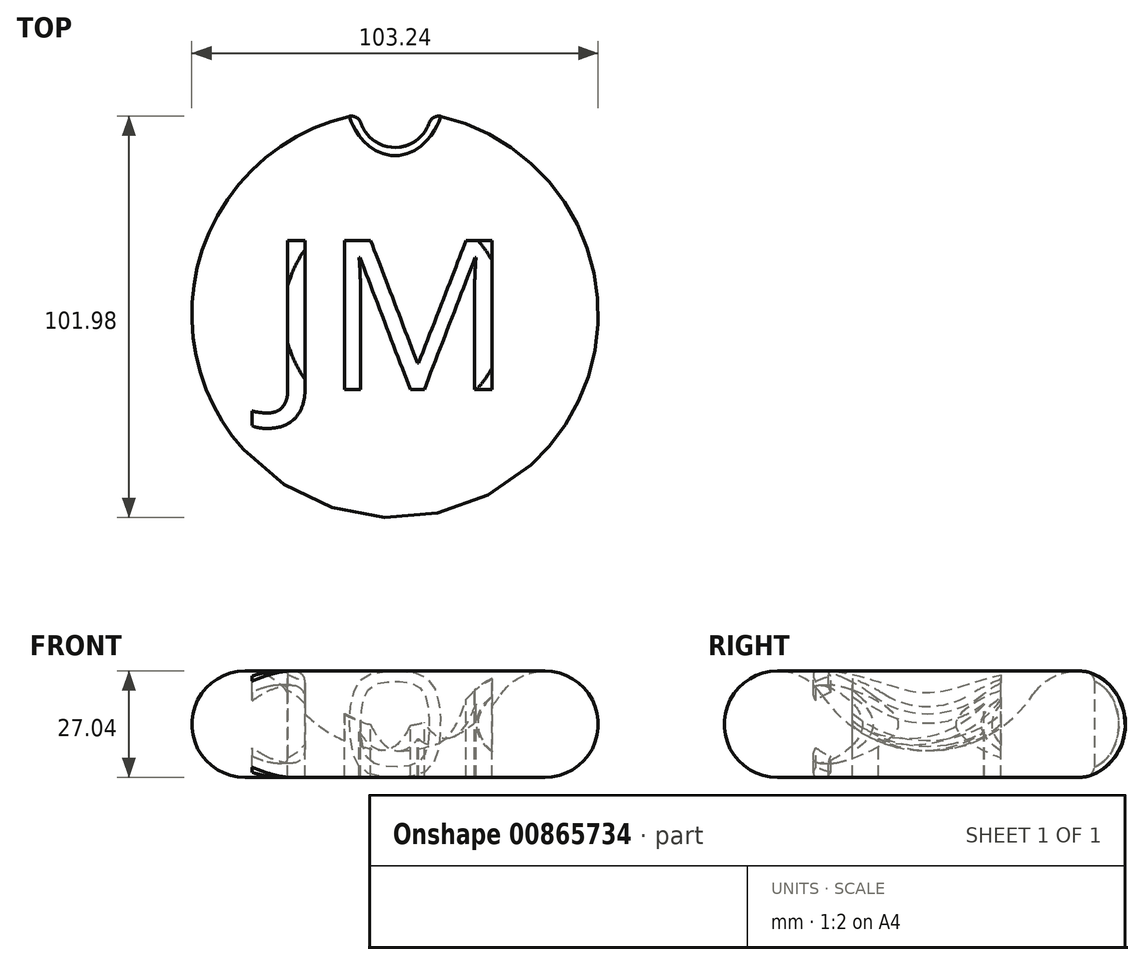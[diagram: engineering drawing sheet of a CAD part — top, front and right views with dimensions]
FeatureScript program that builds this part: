
annotation { "Feature Type Name" : "Feature", "Feature Type Description" : "" }
export const myFeature = defineFeature(function(context is Context, id is Id, definition is map)
    precondition{}
    {
        {
            var Q0;
            Q0=qCreatedBy(makeId("Front.planeOp"),FACE);
            var sketch = newSketch(context, id + "F0", { "sketchPlane" : qUnion([Q0])});
            skArc(sketch, "E0", {"start": v(-26.87, 21.05) * mm, "mid": v(-15.23, 10.52) * mm, "end": v(0, 6.7) * mm});
            skArc(sketch, "E1", {"start": v(-26.87, 21.05) * mm, "mid": v(-50.03, 19.89) * mm, "end": v(-38.1, 0) * mm});
            skLineSegment(sketch, "E2", {"start": v(0, 6.7) * mm, "end": v(0, 0) * mm});
            skLineSegment(sketch, "E3", {"start": v(0, 0) * mm, "end": v(-38.1, 0) * mm});
            skSolve(sketch);
        }
        {
            var Q0;
            Q0=makeQuery(id+"F0.imprint","IMPRINT",FACE,{"disambiguationData":[TD([[makeQuery(id+"F0.imprint","IMPRINT",EDGE,{"derivedFrom":sQuery(id+"F0.wireOp",EDGE,"E0")}),-1.0]])]});
            var Q1;
            Q1=sQuery(id+"F0.wireOp",EDGE,"E2");
            revolve(context, id + "F1", {"surfaceOperationType" : NewSurfaceOperationType.NEW, "entities" : qUnion([Q0]), "axis" : qUnion([Q1]), "revolveType" : RevolveType.FULL});
        }
        {
            var Q0;
            Q0=qCreatedBy(makeId("Top.planeOp"),FACE);
            cPlane(context, id + "F2", {"entities" : qUnion([Q0]), "cplaneType" : CPlaneType.OFFSET, "offset" : 50.8 * mm, "width" : 152.4 * mm, "height" : 152.4 * mm});
        }
        {
            var Q0;
            Q0=qCreatedBy(id+"F2.planeOp",FACE);
            var sketch = newSketch(context, id + "F3", { "sketchPlane" : qUnion([Q0])});
            skText(sketch, "E4", { "text": "JM\n", "fontName": "OpenSans-Regular.ttf"});
            const initialGuessF3  = {"E4": [-0.03215, -0.01905, 1, 0, 0.0381]};
            skSetInitialGuess(sketch, initialGuessF3);
            skSolve(sketch);
        }
        {
            var Q0;
            Q0 = qSketchRegion(id + "F3", true);
            extrude(context, id + "F4", {"entities" : qUnion([Q0]), "operationType" : NewBodyOperationType.REMOVE, "oppositeDirection" : true, "depth" : 76.2 * mm, "offsetDistance" : 25.4 * mm});
        }
        {
            var Q0;
            Q0=qCreatedBy(makeId("Front.planeOp"),FACE);
            var sketch = newSketch(context, id + "F5", { "sketchPlane" : qUnion([Q0])});
            skCircle(sketch, "E5", {"center": v(-38.1, 13.52) * mm, "radius": 9.92 * mm});
            skSolve(sketch);
        }
        {
            var Q0;
            Q0 = qSketchRegion(id + "F5", true);
            var Q1;
            Q1=sQuery(id+"F0.wireOp",EDGE,"E2");
            revolve(context, id + "F6", {"operationType" : NewBodyOperationType.ADD, "surfaceOperationType" : NewSurfaceOperationType.NEW, "entities" : qUnion([Q0]), "axis" : qUnion([Q1]), "revolveType" : RevolveType.FULL});
        }
        {
            var Q0;
            Q0=qCreatedBy(makeId("Top.planeOp"),FACE);
            var sketch = newSketch(context, id + "F7", { "sketchPlane" : qUnion([Q0])});
            skCircle(sketch, "E6", {"center": v(0, 51.55) * mm, "radius": 9.15 * mm});
            skSolve(sketch);
        }
        {
            var Q0;
            Q0 = qSketchRegion(id + "F7", true);
            extrude(context, id + "F8", {"entities" : qUnion([Q0]), "operationType" : NewBodyOperationType.REMOVE, "depth" : 30.23 * mm, "offsetDistance" : 25.4 * mm});
        }
        {
            var Q0;
            Q0=makeQuery(id+"F8.boolean.opBoolean","INTERSECT",EDGE,{"derivedFrom":[makeQuery(id+"F1.opRevolve","SWEPT_FACE",FACE,{"disambiguationData":[OSD([sQuery(id+"F0.wireOp",EDGE,"E1")])]}),makeQuery(id+"F8.opExtrude","SWEPT_FACE",FACE,{"disambiguationData":[OSD([sQuery(id+"F7.wireOp",EDGE,"E6")])]})]});
            fillet(context, id + "F9", {"entities" : qUnion([Q0]), "radius" : 2.54 * mm, "tangentPropagation" : true, "allowEdgeOverflow" : false});
        }
    });
